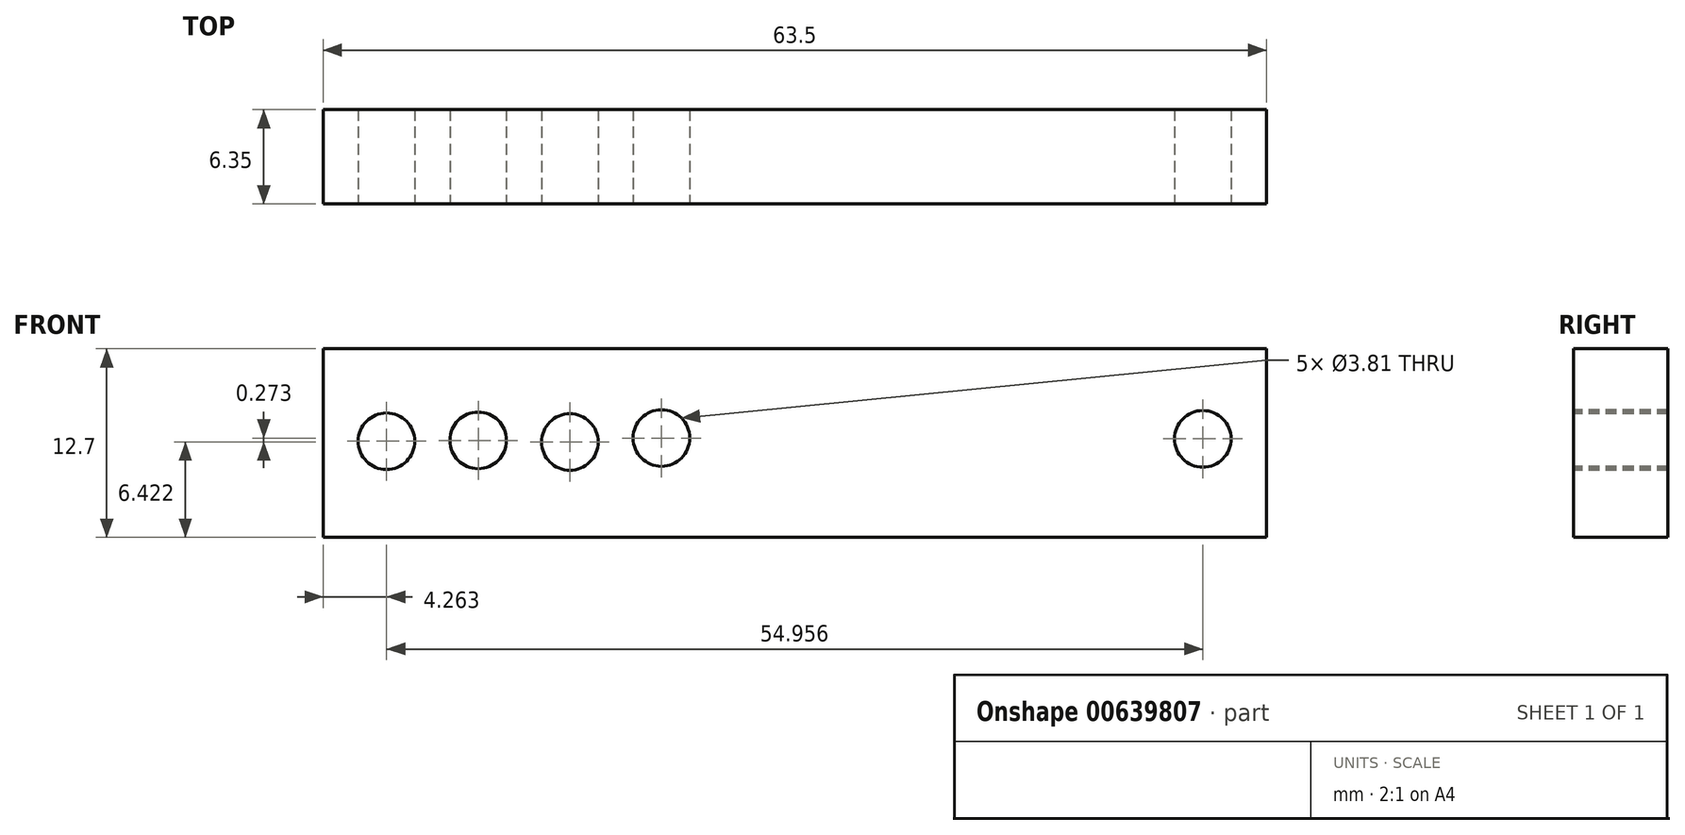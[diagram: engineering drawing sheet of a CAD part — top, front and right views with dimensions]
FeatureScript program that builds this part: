
annotation { "Feature Type Name" : "Feature", "Feature Type Description" : "" }
export const myFeature = defineFeature(function(context is Context, id is Id, definition is map)
    precondition{}
    {
        {
            var Q0;
            Q0=qCreatedBy(makeId("Front.planeOp"),FACE);
            var sketch = newSketch(context, id + "F0", { "sketchPlane" : qUnion([Q0])});
            skLineSegment(sketch, "E0.bottom", {"start": v(-34.77, 16.42) * mm, "end": v(28.73, 16.42) * mm});
            skLineSegment(sketch, "E0.top", {"start": v(-34.77, 3.72) * mm, "end": v(28.73, 3.72) * mm});
            skLineSegment(sketch, "E0.left", {"start": v(-34.77, 16.42) * mm, "end": v(-34.77, 3.72) * mm});
            skLineSegment(sketch, "E0.right", {"start": v(28.73, 16.42) * mm, "end": v(28.73, 3.72) * mm});
            skCircle(sketch, "E1", {"center": v(24.45, 10.36) * mm, "radius": 1.9 * mm});
            skCircle(sketch, "E2", {"center": v(-30.5, 10.2) * mm, "radius": 1.9 * mm});
            skCircle(sketch, "E3", {"center": v(-24.33, 10.26) * mm, "radius": 1.9 * mm});
            skCircle(sketch, "E4", {"center": v(-18.16, 10.14) * mm, "radius": 1.9 * mm});
            skCircle(sketch, "E5", {"center": v(-12, 10.41) * mm, "radius": 1.9 * mm});
            skSolve(sketch);
        }
        {
            var Q0;
            Q0=makeQuery(id+"F0.imprint","IMPRINT",FACE,{"disambiguationData":[TD([[makeQuery(id+"F0.imprint","IMPRINT",EDGE,{"derivedFrom":sQuery(id+"F0.wireOp",EDGE,"E0.bottom")}),-1.0]])]});
            extrude(context, id + "F1", {"entities" : qUnion([Q0]), "oppositeDirection" : true, "depth" : 6.35 * mm, "offsetDistance" : 25.4 * mm});
        }
    });
